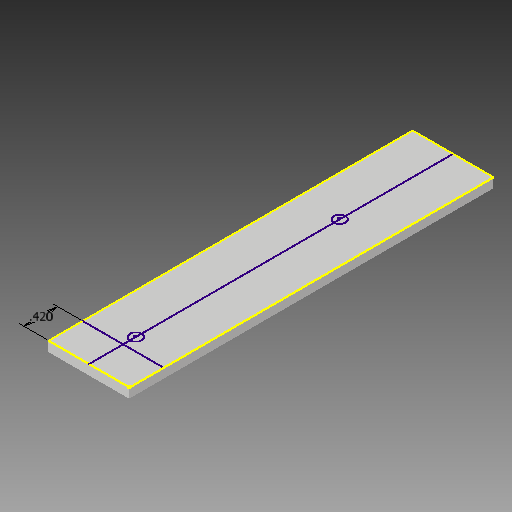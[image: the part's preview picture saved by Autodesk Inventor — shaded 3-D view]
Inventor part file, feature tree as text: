
AUTODESK INVENTOR PART (.ipt)
format: ipt  version: 2017 (Build 210142000, 142)  size: 87,552 bytes
history: native  units: in
note: dims shown in document units (in); Inventor stores cm internally (conversion verified against a paired STEP export)
features: sketch x4, other x3, reference x2, extrude x1
ambient origin geometry x8: Origin, YZ Plane, XZ Plane, XY Plane, X Axis, Y Axis, Z Axis, Center Point
bodies: Solid1 (feature_tree)
feature tree (10):
  extrude  "Extrusion1"  Depth=1.0in
  sketch  "Sketch2"  dims[d2=0.125in d3=0.0in]
  sketch  "Sketch3"  dims[d4=0.42in]
  sketch  "Sketch4"
  sketch  "Sketch1"  dims[d0=4.5in d1=1.0in]
  reference  "Reference1"
  reference  "Reference2"
  other  "<userpath>\Documents\GitHub\RobotuxCAD\Team Robotux 15-16 Robot Cad Assets\Pickup 16.iam"
  other  "Pickup 16.iam"
  other  "tetrix_739089_2012:1"
